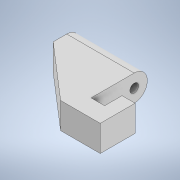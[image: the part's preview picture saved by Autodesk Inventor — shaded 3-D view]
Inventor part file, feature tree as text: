
AUTODESK INVENTOR PART (.ipt)
format: ipt  version: 2022 (Build 260153000, 153)  size: 134,144 bytes
history: native  units: in
note: dims shown in document units (in); Inventor stores cm internally (conversion verified against a paired STEP export)
features: extrude x3, sketch x3
ambient origin geometry x8: Origin, YZ Plane, XZ Plane, XY Plane, X Axis, Y Axis, Z Axis, Center Point
bodies: Solid1 (feature_tree)
feature tree (6):
  extrude  "Extrusion1"  Depth=0.122in
  extrude  "Extrusion2"  Depth=0.1181in
  extrude  "Extrusion3"  Depth=0.2362in TaperAngle=0.0deg
  sketch  "Sketch1"  dims[d1=0.6693in d2=0.122in]
  sketch  "Sketch2"  dims[d3=0.1181in d4=0.1181in]
  sketch  "Sketch3"  dims[d5=0.2441in d6=0.2362in d7=0.0in d8=0.122in d9=0.0787in d10=0.2362in d11=0.0in d13=0.315in d14=0.3937in d15=0.0in d17=0.5118in d18=0.4921in]
